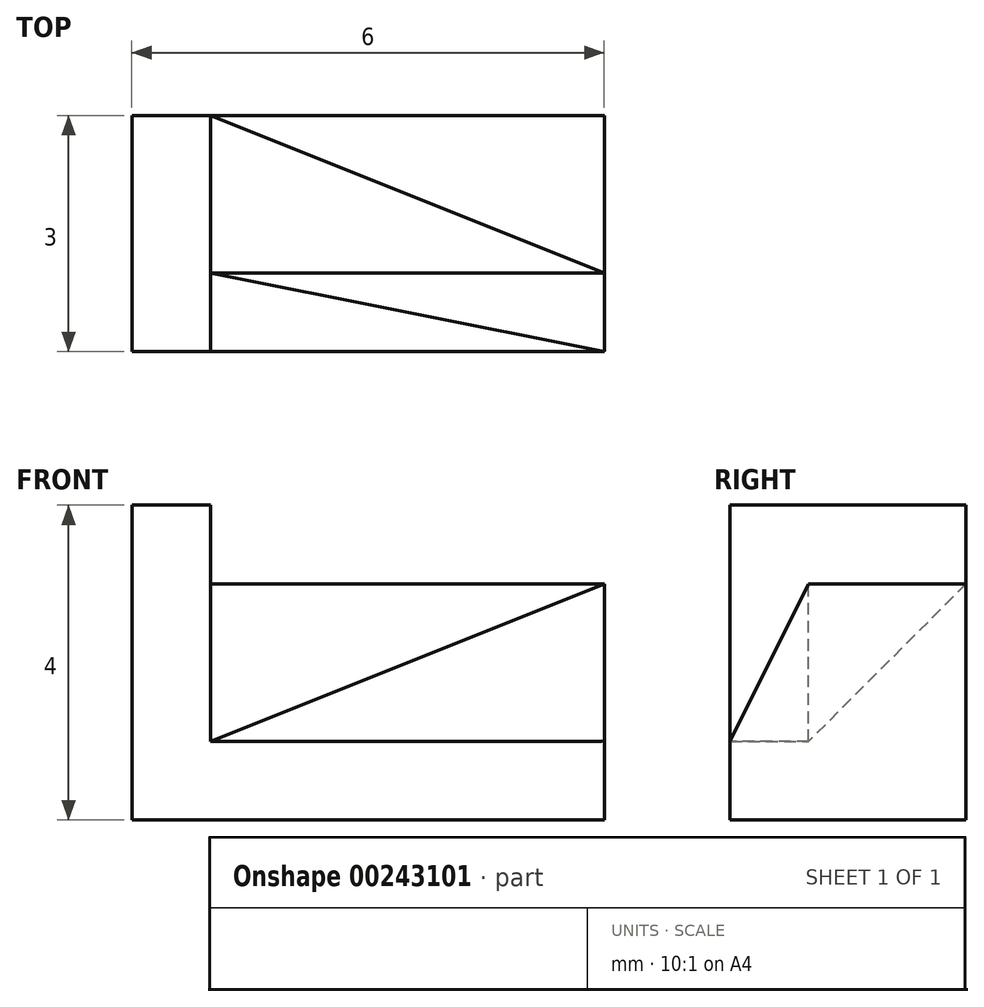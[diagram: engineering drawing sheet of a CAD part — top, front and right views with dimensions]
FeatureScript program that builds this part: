
annotation { "Feature Type Name" : "Feature", "Feature Type Description" : "" }
export const myFeature = defineFeature(function(context is Context, id is Id, definition is map)
    precondition{}
    {
        {
            var Q0;
            Q0=qCreatedBy(makeId("Top.planeOp"),FACE);
            var sketch = newSketch(context, id + "F0", { "sketchPlane" : qUnion([Q0])});
            skLineSegment(sketch, "E0.bottom", {"start": v(11.08, 10.86) * mm, "end": v(16.08, 10.86) * mm});
            skLineSegment(sketch, "E0.top", {"start": v(11.08, 7.86) * mm, "end": v(16.08, 7.86) * mm});
            skLineSegment(sketch, "E0.left", {"start": v(11.08, 10.86) * mm, "end": v(11.08, 7.86) * mm});
            skLineSegment(sketch, "E0.right", {"start": v(16.08, 10.86) * mm, "end": v(16.08, 7.86) * mm});
            skSolve(sketch);
        }
        {
            var Q0;
            Q0=qCreatedBy(makeId("Top.planeOp"),FACE);
            var sketch = newSketch(context, id + "F1", { "sketchPlane" : qUnion([Q0])});
            skLineSegment(sketch, "E1.0", {"start": v(11.08, 10.86) * mm, "end": v(11.08, 7.86) * mm});
            skLineSegment(sketch, "E2.0", {"start": v(11.08, 7.86) * mm, "end": v(16.08, 7.86) * mm});
            skLineSegment(sketch, "E3.bottom", {"start": v(11.08, 10.86) * mm, "end": v(16.08, 10.86) * mm});
            skLineSegment(sketch, "E3.right", {"start": v(16.08, 10.86) * mm, "end": v(16.08, 7.86) * mm});
            skSolve(sketch);
        }
        {
            var Q0;
            Q0 = qSketchRegion(id + "F0", true);
            extrude(context, id + "F2", {"entities" : qUnion([Q0]), "depth" : 3 * mm});
        }
        {
            var Q0;
            Q0=makeQuery(id+"F2.opExtrude","SWEPT_FACE",FACE,{"disambiguationData":[OSD([sQuery(id+"F0.wireOp",EDGE,"E0.left")])]});
            var sketch = newSketch(context, id + "F3", { "sketchPlane" : qUnion([Q0])});
            skLineSegment(sketch, "E4", {"start": v(-7.86, 0) * mm, "end": v(-7.86, 1) * mm, "construction": true});
            skLineSegment(sketch, "E5", {"start": v(-7.86, 1) * mm, "end": v(-8.86, 1) * mm, "construction": true});
            skSolve(sketch);
        }
        {
            var Q0;
            Q0=makeQuery(id+"F2.opExtrude","SWEPT_FACE",FACE,{"disambiguationData":[OSD([sQuery(id+"F0.wireOp",EDGE,"E0.top")])]});
            var sketch = newSketch(context, id + "F4", { "sketchPlane" : qUnion([Q0])});
            skLineSegment(sketch, "E6", {"start": v(16.08, 0) * mm, "end": v(16.08, 1) * mm, "construction": true});
            skSolve(sketch);
        }
        {
            var Q0;
            Q0=sQuery(id+"F4.wireOp",VERTEX,"E6.end");
            var Q1;
            Q1=sQuery(id+"F3.wireOp",VERTEX,"E5.start");
            var Q2;
            Q2=sQuery(id+"F3.wireOp",VERTEX,"E5.end");
            cPlane(context, id + "F5", {"entities" : qUnion([Q0, Q1, Q2]), "cplaneType" : CPlaneType.THREE_POINT, "offset" : 25 * mm, "width" : 150 * mm, "height" : 150 * mm});
        }
        {
            var Q0;
            Q0=qCreatedBy(id+"F5.planeOp",FACE);
            var sketch = newSketch(context, id + "F6", { "sketchPlane" : qUnion([Q0])});
            skPoint(sketch, "E7.0", {"position": v(11.08, 8.86) * mm});
            skPoint(sketch, "E8.0", {"position": v(11.08, 7.86) * mm});
            skPoint(sketch, "E9.0", {"position": v(16.08, 7.86) * mm});
            skLineSegment(sketch, "E10", {"start": v(11.08, 8.86) * mm, "end": v(16.08, 7.86) * mm});
            skLineSegment(sketch, "E11", {"start": v(16.12, 7.87) * mm, "end": v(11.08, 7.86) * mm});
            skLineSegment(sketch, "E12", {"start": v(11.08, 7.86) * mm, "end": v(11.08, 8.86) * mm});
            skSolve(sketch);
        }
        {
            var Q0;
            Q0 = qSketchRegion(id + "F6", true);
            extrude(context, id + "F7", {"entities" : qUnion([Q0]), "operationType" : NewBodyOperationType.REMOVE, "depth" : 25 * mm});
        }
        {
            var Q0;
            Q0=makeQuery(id+"F2.opExtrude","CAP_FACE",FACE,{"disambiguationData":[OSD([sQuery(id+"F0.wireOp",EDGE,"E0.bottom"),sQuery(id+"F0.wireOp",EDGE,"E0.top"),sQuery(id+"F0.wireOp",EDGE,"E0.left"),sQuery(id+"F0.wireOp",EDGE,"E0.right")])],"isStart":false});
            var sketch = newSketch(context, id + "F8", { "sketchPlane" : qUnion([Q0])});
            skLineSegment(sketch, "E13", {"start": v(11.08, 10.86) * mm, "end": v(16.08, 8.86) * mm});
            skLineSegment(sketch, "E14", {"start": v(16.08, 8.86) * mm, "end": v(16.08, 10.86) * mm});
            skLineSegment(sketch, "E15", {"start": v(16.08, 10.86) * mm, "end": v(11.08, 10.86) * mm});
            skSolve(sketch);
        }
        {
            var Q0;
            Q0=makeQuery(id+"F2.opExtrude","SWEPT_FACE",FACE,{"disambiguationData":[OSD([sQuery(id+"F0.wireOp",EDGE,"E0.left")])]});
            var sketch = newSketch(context, id + "F9", { "sketchPlane" : qUnion([Q0])});
            skLineSegment(sketch, "E16", {"start": v(-10.86, 3) * mm, "end": v(-8.86, 3) * mm, "construction": true});
            skLineSegment(sketch, "E17", {"start": v(-8.86, 3) * mm, "end": v(-8.86, 1) * mm, "construction": true});
            skSolve(sketch);
        }
        {
            var Q0;
            Q0=sQuery(id+"F9.wireOp",VERTEX,"E16.start");
            var Q1;
            Q1=sQuery(id+"F9.wireOp",VERTEX,"E17.end");
            var Q2;
            Q2=sQuery(id+"F8.wireOp",VERTEX,"E14.start");
            cPlane(context, id + "F10", {"entities" : qUnion([Q0, Q1, Q2]), "cplaneType" : CPlaneType.THREE_POINT, "offset" : 25 * mm, "width" : 150 * mm, "height" : 150 * mm});
        }
        {
            var Q0;
            Q0=qCreatedBy(id+"F10.planeOp",FACE);
            var sketch = newSketch(context, id + "F11", { "sketchPlane" : qUnion([Q0])});
            skLineSegment(sketch, "E18.0", {"start": v(-9.15, 9.8) * mm, "end": v(-14.35, 8.39) * mm});
            skLineSegment(sketch, "E19", {"start": v(-9.15, 9.8) * mm, "end": v(-9.15, 6.97) * mm});
            skLineSegment(sketch, "E20", {"start": v(-9.15, 6.97) * mm, "end": v(-14.35, 8.39) * mm});
            skLineSegment(sketch, "E21", {"start": v(-14.35, 8.39) * mm, "end": v(-9.15, 9.8) * mm});
            skSolve(sketch);
        }
        {
            var Q0;
            Q0 = qSketchRegion(id + "F11", true);
            extrude(context, id + "F12", {"entities" : qUnion([Q0]), "operationType" : NewBodyOperationType.REMOVE, "oppositeDirection" : true, "depth" : 25 * mm});
        }
        {
            var Q0;
            Q0=makeQuery(id+"F2.opExtrude","SWEPT_FACE",FACE,{"disambiguationData":[OSD([sQuery(id+"F0.wireOp",EDGE,"E0.right")])]});
            var sketch = newSketch(context, id + "F13", { "sketchPlane" : qUnion([Q0])});
            skLineSegment(sketch, "E22", {"start": v(8.86, 3) * mm, "end": v(7.86, 1) * mm});
            skLineSegment(sketch, "E23", {"start": v(7.86, 1) * mm, "end": v(7.86, 0) * mm});
            skSolve(sketch);
        }
        {
            var Q0;
            Q0=sQuery(id+"F13.wireOp",VERTEX,"E23.start");
            var Q1;
            Q1=sQuery(id+"F13.wireOp",VERTEX,"E22.start");
            var Q2;
            Q2=sQuery(id+"F9.wireOp",VERTEX,"E17.end");
            cPlane(context, id + "F14", {"entities" : qUnion([Q0, Q1, Q2]), "cplaneType" : CPlaneType.THREE_POINT, "offset" : 25 * mm, "width" : 150 * mm, "height" : 150 * mm});
        }
        {
            var Q0;
            Q0=qCreatedBy(id+"F14.planeOp",FACE);
            var sketch = newSketch(context, id + "F15", { "sketchPlane" : qUnion([Q0])});
            skLineSegment(sketch, "E24.0", {"start": v(-14.67, 6.65) * mm, "end": v(-14.67, 4.4) * mm});
            skLineSegment(sketch, "E25", {"start": v(-9.6, 4.86) * mm, "end": v(-14.67, 6.65) * mm});
            skLineSegment(sketch, "E26", {"start": v(-14.67, 4.4) * mm, "end": v(-14.67, 6.65) * mm});
            skLineSegment(sketch, "E27", {"start": v(-14.67, 4.4) * mm, "end": v(-9.6, 4.86) * mm});
            skLineSegment(sketch, "E28", {"start": v(-9.6, 4.86) * mm, "end": v(-9.8, 7.3) * mm});
            skLineSegment(sketch, "E29", {"start": v(-9.8, 7.3) * mm, "end": v(-14.67, 6.65) * mm});
            skLineSegment(sketch, "E30", {"start": v(-14.67, 6.65) * mm, "end": v(-15.47, 6.54) * mm});
            skLineSegment(sketch, "E31", {"start": v(-15.47, 6.54) * mm, "end": v(-15.47, 4.4) * mm});
            skLineSegment(sketch, "E32", {"start": v(-15.47, 4.4) * mm, "end": v(-14.67, 4.4) * mm});
            skSolve(sketch);
        }
        {
            var Q0;
            Q0 = qSketchRegion(id + "F15", true);
            extrude(context, id + "F16", {"entities" : qUnion([Q0]), "operationType" : NewBodyOperationType.REMOVE, "oppositeDirection" : true, "depth" : 25 * mm});
        }
        {
            var Q0;
            Q0=qCreatedBy(makeId("Top.planeOp"),FACE);
            var sketch = newSketch(context, id + "F17", { "sketchPlane" : qUnion([Q0])});
            skLineSegment(sketch, "E33.0", {"start": v(11.08, 10.86) * mm, "end": v(11.08, 7.86) * mm});
            skLineSegment(sketch, "E34.bottom", {"start": v(11.08, 10.86) * mm, "end": v(11.08, 10.86) * mm});
            skLineSegment(sketch, "E34.top", {"start": v(11.08, 7.86) * mm, "end": v(11.08, 7.86) * mm});
            skLineSegment(sketch, "E35.bottom", {"start": v(11.08, 10.86) * mm, "end": v(10.08, 10.86) * mm});
            skLineSegment(sketch, "E35.top", {"start": v(11.08, 7.86) * mm, "end": v(10.08, 7.86) * mm});
            skLineSegment(sketch, "E35.right", {"start": v(10.08, 10.86) * mm, "end": v(10.08, 7.86) * mm});
            skSolve(sketch);
        }
        {
            var Q0;
            Q0 = qSketchRegion(id + "F17", true);
            extrude(context, id + "F18", {"entities" : qUnion([Q0]), "operationType" : NewBodyOperationType.ADD, "depth" : 4 * mm});
        }
    });
